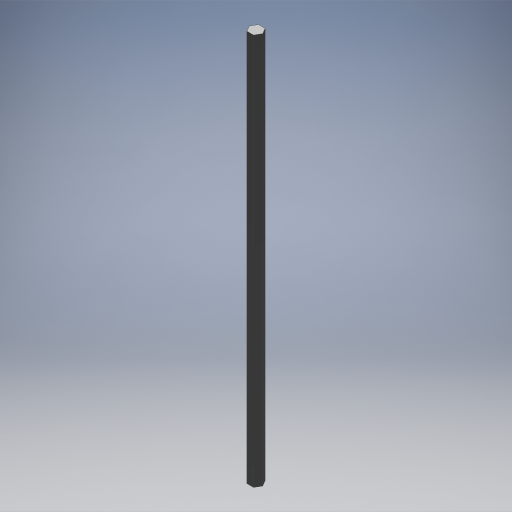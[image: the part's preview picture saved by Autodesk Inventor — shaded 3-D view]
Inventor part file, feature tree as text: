
AUTODESK INVENTOR PART (.ipt)
format: ipt  version: 2024.2 (Build 282272000, 272)  size: 453,120 bytes
history: native  units: in
note: dims shown in document units (in); Inventor stores cm internally (conversion verified against a paired STEP export)
features: extrude x32, other x4, hole x2
ambient origin geometry x8: Origin, YZ Plane, XZ Plane, XY Plane, X Axis, Y Axis, Z Axis, Center Point
bodies: Solid3 (feature_tree)
feature tree (38):
  extrude  "BaseProfile625Round"  Depth=0.5in
  extrude  "BaseProfileRoundTube"  Depth=0.5413in
  extrude  "BaseProfile500Hex"  Depth=0.5in
  extrude  "BaseProfile500Thunderhex"  Depth=0.375in
  extrude  "BaseProfile500Round"  Depth=0.4035in
  extrude  "BaseProfile375Hex"  Depth=0.75in
  extrude  "BaseProfile375Thunderhex"  Depth=0.468in
  extrude  "BaseProfile375Round"  Depth=0.201in
  extrude  "TopShaftProfile1Hex500"  Depth=0.159in
  extrude  "TopShaftProfile1ThunderHex500"  Depth=0.25in
  extrude  "TopShaftProfile1Round500"  Depth=36.0in TaperAngle=0.0deg
  extrude  "TopShaftProfile1Hex375"  Depth=17.0in TaperAngle=0.0deg
  extrude  "TopShaftProfile1ThunderHex375"  Depth=36.0in TaperAngle=0.0deg
  extrude  "TopShaftProfile1Round375"  Depth=36.0in TaperAngle=0.0deg
  extrude  "TopShaftProfile2ThunderHex500"  Depth=36.0in TaperAngle=0.0deg
  extrude  "TopShaftProfile2Round500"  Depth=36.0in TaperAngle=0.0deg
  extrude  "TopShaftProfile2Hex375"  Depth=36.0in TaperAngle=0.0deg
  extrude  "TopShaftProfile2ThunderHex375"  Depth=36.0in TaperAngle=0.0deg
  extrude  "TopShaftProfile2Round375"  Depth=36.0in TaperAngle=0.0deg
  other  "TopRetentionGroove&BearingRound"
  hole  "TopShaftTappedHole"  [1 undecoded]
  other  "TopShaftThread"
  extrude  "BottomShaftProfile1Hex500"  TaperAngle=0.0deg  [1 undecoded]
  extrude  "BottomShaftProfile1ThunderHex500"  TaperAngle=0.0deg  [1 undecoded]
  extrude  "BottomShaftProfile1Round500"  TaperAngle=0.0deg  [1 undecoded]
  extrude  "BottomShaftProfile1Hex375"  TaperAngle=0.0deg  [1 undecoded]
  extrude  "BottomShaftProfile1ThunderHex375"  TaperAngle=0.0deg  [1 undecoded]
  extrude  "BottomShaftProfile2ThunderHex500"  TaperAngle=0.0deg  [1 undecoded]
  extrude  "BottomShaftProfile1Round375"  TaperAngle=0.0deg  [1 undecoded]
  extrude  "BottomShaftProfile2Round500"  TaperAngle=0.0deg  [1 undecoded]
  extrude  "BottomShaftProfile2Hex375"  TaperAngle=0.0deg  [1 undecoded]
  extrude  "BottomShaftProfile2ThunderHex375"  TaperAngle=0.0deg  [1 undecoded]
  extrude  "BottomShaftProfile2Round375"  TaperAngle=0.0deg  [1 undecoded]
  hole  "BottomShaftTappedHole"  [1 undecoded]
  other  "BottomShaftThread"
  other  "BottomRetentionGroove&BearingRound"
  extrude  "BaseProfile375ThunderhexHole"  TaperAngle=0.0deg  [1 undecoded]
  extrude  "BaseProfile500ThunderhexHole"  TaperAngle=0.0deg  [1 undecoded]
note: 15 required parameter values undecoded (feature->parameter linkage not recoverable at this tier; creation-order binding heuristic only, values carry confidence <= 0.55)
